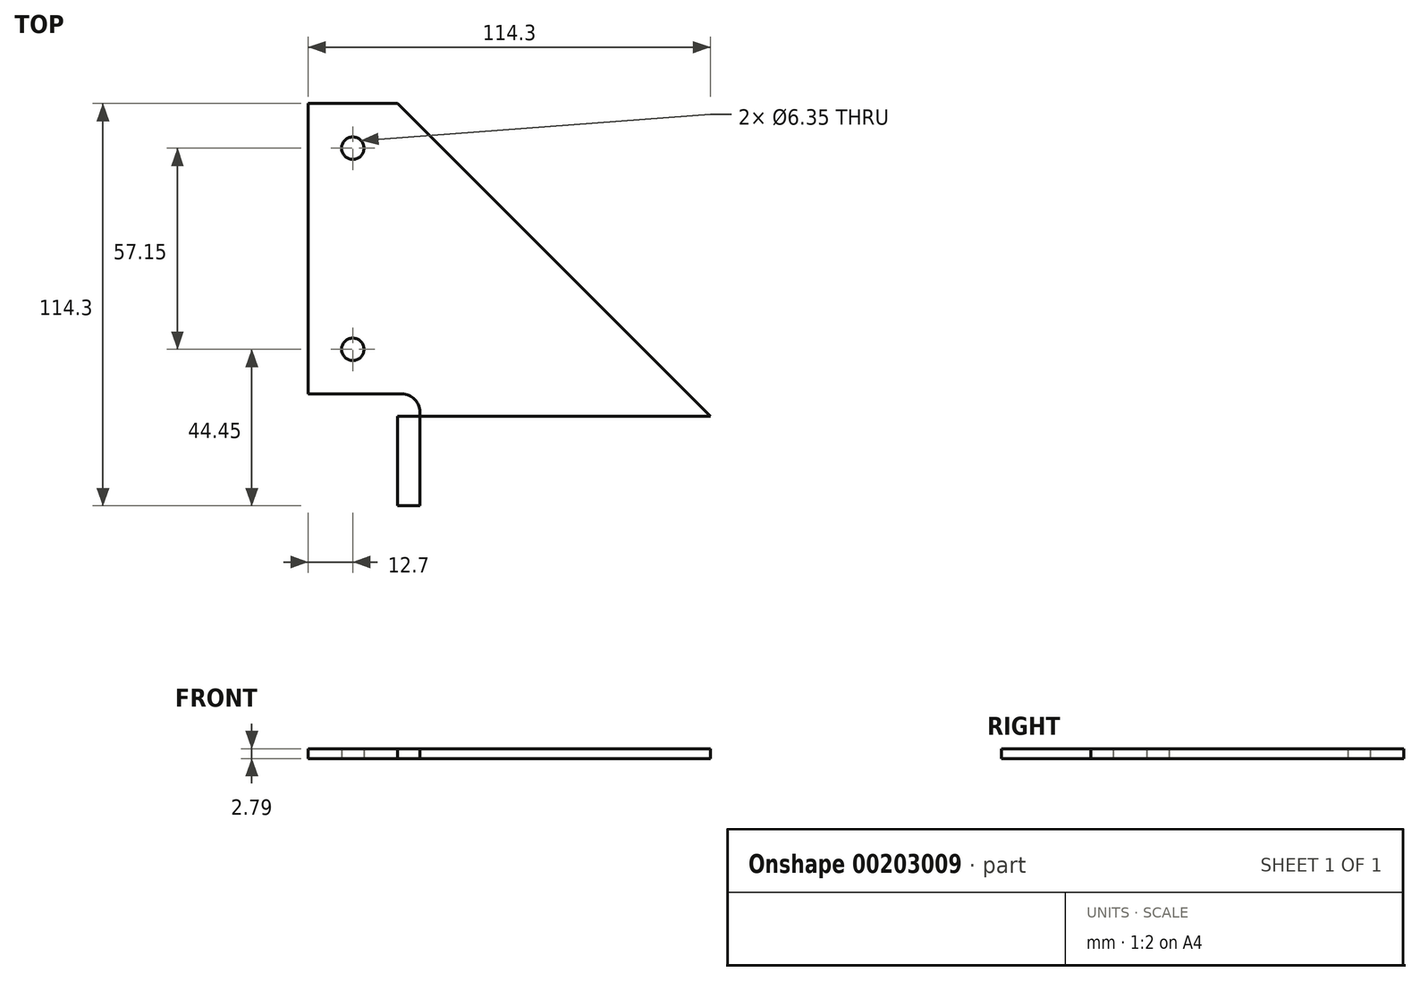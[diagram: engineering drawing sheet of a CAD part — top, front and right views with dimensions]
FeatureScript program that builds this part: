
annotation { "Feature Type Name" : "Feature", "Feature Type Description" : "" }
export const myFeature = defineFeature(function(context is Context, id is Id, definition is map)
    precondition{}
    {
        {
            var Q0;
            Q0=qCreatedBy(makeId("Top.planeOp"),FACE);
            var sketch = newSketch(context, id + "F0", { "sketchPlane" : qUnion([Q0])});
            skLineSegment(sketch, "E0.bottom", {"start": v(0, 0) * mm, "end": v(25.4, 0) * mm});
            skLineSegment(sketch, "E0.top", {"start": v(0, 114.3) * mm, "end": v(25.4, 114.3) * mm});
            skLineSegment(sketch, "E0.left", {"start": v(0, 0) * mm, "end": v(0, 114.3) * mm});
            skLineSegment(sketch, "E0.right", {"start": v(25.4, 0) * mm, "end": v(25.4, 114.3) * mm});
            skLineSegment(sketch, "E1.bottom", {"start": v(0, 0) * mm, "end": v(114.3, 0) * mm});
            skLineSegment(sketch, "E1.top", {"start": v(0, 25.4) * mm, "end": v(114.3, 25.4) * mm});
            skLineSegment(sketch, "E1.left", {"start": v(0, 0) * mm, "end": v(0, 25.4) * mm});
            skLineSegment(sketch, "E1.right", {"start": v(114.3, 0) * mm, "end": v(114.3, 25.4) * mm});
            skLineSegment(sketch, "E2", {"start": v(25.4, 114.3) * mm, "end": v(114.3, 25.4) * mm});
            skLineSegment(sketch, "E3.bottom", {"start": v(0, 0) * mm, "end": v(31.75, 0) * mm});
            skLineSegment(sketch, "E3.top", {"start": v(0, 31.75) * mm, "end": v(31.75, 31.75) * mm});
            skLineSegment(sketch, "E3.left", {"start": v(0, 0) * mm, "end": v(0, 31.75) * mm});
            skLineSegment(sketch, "E3.right", {"start": v(31.75, 0) * mm, "end": v(31.75, 31.75) * mm});
            skCircle(sketch, "E4", {"center": v(12.7, 146.05) * mm, "radius": 3.18 * mm});
            skPoint(sketch, "E4.centerSnap0", {"position": v(12.7, 114.3) * mm});
            skCircle(sketch, "E5", {"center": v(12.7, 44.45) * mm, "radius": 3.18 * mm});
            skCircle(sketch, "E6", {"center": v(101.6, 12.7) * mm, "radius": 3.18 * mm});
            skPoint(sketch, "E6.centerSnap0", {"position": v(114.3, 12.7) * mm});
            skCircle(sketch, "E7", {"center": v(44.45, 12.7) * mm, "radius": 3.18 * mm});
            skCircle(sketch, "E8", {"center": v(12.7, 101.6) * mm, "radius": 3.18 * mm});
            skSolve(sketch);
        }
        {
            var Q0;
            {var subQ7=sQuery(id+"F0.wireOp",EDGE,"E2");Q0=makeQuery(id+"F0.imprint","IMPRINT",FACE,{"disambiguationData":[TD([[makeQuery(id+"F0.imprint","IMPRINT",EDGE,{"derivedFrom":subQ7}),-1.0]])]});}
            var Q1;
            {var subQ1=sQuery(id+"F0.wireOp",EDGE,"E1.bottom");Q1=makeQuery(id+"F0.imprint","IMPRINT",FACE,{"disambiguationData":[TD([[makeQuery(id+"F0.imprint","IMPRINT",EDGE,{"derivedFrom":subQ1}),1.0]])]});}
            var Q2;
            {var subQ4=sQuery(id+"F0.wireOp",EDGE,"E0.top");Q2=makeQuery(id+"F0.imprint","IMPRINT",FACE,{"disambiguationData":[TD([[makeQuery(id+"F0.imprint","IMPRINT",EDGE,{"derivedFrom":subQ4}),-1.0]])]});}
            extrude(context, id + "F1", {"entities" : qUnion([Q0, Q1, Q2]), "depth" : 2.8 * mm});
        }
        {
            var Q0;
            Q0=makeQuery(id+"F1.opExtrude","SWEPT_EDGE",EDGE,{"disambiguationData":[OSD([sQuery(id+"F0.wireOp",EDGE,"E3.top"),sQuery(id+"F0.wireOp",EDGE,"E3.right")])]});
            fillet(context, id + "F2", {"entities" : qUnion([Q0]), "radius" : 5.08 * mm, "tangentPropagation" : true, "allowEdgeOverflow" : false});
        }
    });
